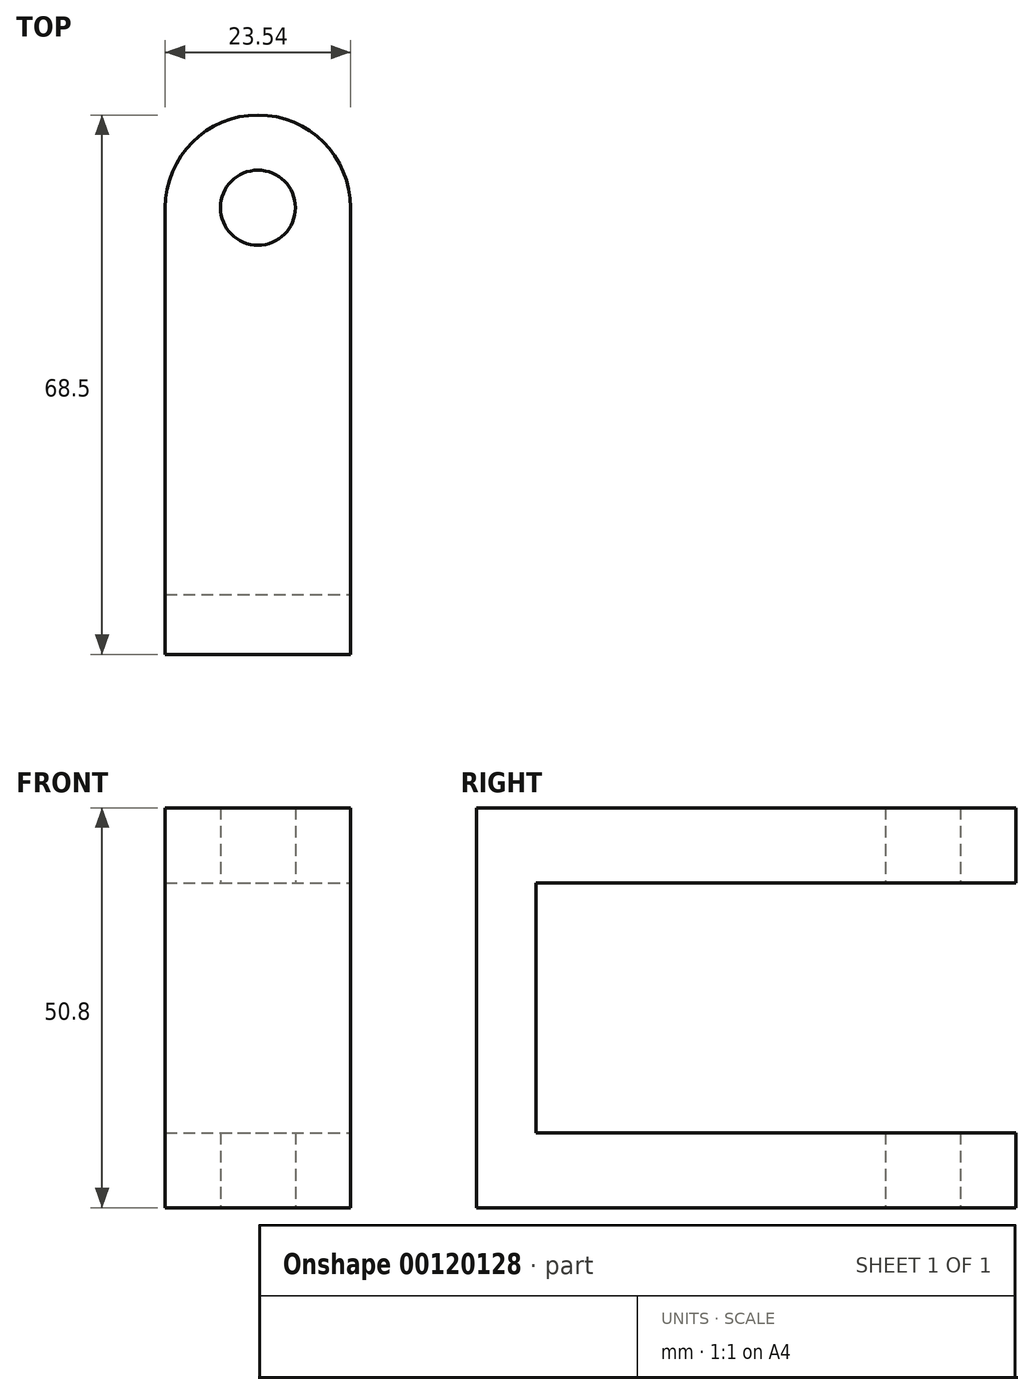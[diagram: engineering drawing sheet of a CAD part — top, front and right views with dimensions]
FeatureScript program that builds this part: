
annotation { "Feature Type Name" : "Feature", "Feature Type Description" : "" }
export const myFeature = defineFeature(function(context is Context, id is Id, definition is map)
    precondition{}
    {
        {
            var Q0;
            Q0=qCreatedBy(makeId("Top.planeOp"),FACE);
            var sketch = newSketch(context, id + "F0", { "sketchPlane" : qUnion([Q0])});
            skLineSegment(sketch, "E0.bottom", {"start": v(-11.77, -56.73) * mm, "end": v(11.77, -56.73) * mm});
            skLineSegment(sketch, "E0.top", {"start": v(-11.77, 0) * mm, "end": v(11.77, 0) * mm, "construction": true});
            skLineSegment(sketch, "E0.left", {"start": v(-11.77, -56.73) * mm, "end": v(-11.77, 0) * mm});
            skLineSegment(sketch, "E0.right", {"start": v(11.77, -56.73) * mm, "end": v(11.77, 0) * mm});
            skArc(sketch, "E1", {"start": v(11.77, 0) * mm, "mid": v(0, 11.77) * mm, "end": v(-11.77, 0) * mm});
            skCircle(sketch, "E2", {"center": v(0, 0) * mm, "radius": 4.76 * mm});
            skSolve(sketch);
        }
        {
            var Q0;
            Q0=makeQuery(id+"F0.imprint","IMPRINT",FACE,{"disambiguationData":[TD([[makeQuery(id+"F0.imprint","IMPRINT",EDGE,{"derivedFrom":sQuery(id+"F0.wireOp",EDGE,"E0.bottom")}),1.0]])]});
            extrude(context, id + "F1", {"entities" : qUnion([Q0]), "depth" : 50.8 * mm});
        }
        {
            var Q0;
            Q0=makeQuery(id+"F1.opExtrude","SWEPT_FACE",FACE,{"disambiguationData":[OSD([sQuery(id+"F0.wireOp",EDGE,"E0.right")])]});
            var sketch = newSketch(context, id + "F2", { "sketchPlane" : qUnion([Q0])});
            skLineSegment(sketch, "E3.bottom", {"start": v(-49.15, 41.28) * mm, "end": v(18.1, 41.28) * mm});
            skLineSegment(sketch, "E3.top", {"start": v(-49.15, 9.52) * mm, "end": v(18.1, 9.52) * mm});
            skLineSegment(sketch, "E3.left", {"start": v(-49.15, 41.28) * mm, "end": v(-49.15, 9.52) * mm});
            skLineSegment(sketch, "E3.right", {"start": v(18.1, 41.28) * mm, "end": v(18.1, 9.52) * mm});
            skLineSegment(sketch, "E4", {"start": v(-35.74, 41.28) * mm, "end": v(-35.74, 50.8) * mm});
            skLineSegment(sketch, "E5", {"start": v(-35.74, 9.52) * mm, "end": v(-35.74, 0) * mm});
            skSolve(sketch);
        }
        {
            var Q0;
            {var subQ4=sQuery(id+"F2.wireOp",EDGE,"E3.left");Q0=makeQuery(id+"F2.imprint","IMPRINT",FACE,{"disambiguationData":[TD([[makeQuery(id+"F2.imprint","IMPRINT",EDGE,{"derivedFrom":subQ4}),1.0]])]});}
            var Q1;
            {var subQ0=sQuery(id+"F2.wireOp",EDGE,"E3.right");Q1=makeQuery(id+"F2.imprint","IMPRINT",FACE,{"disambiguationData":[TD([[makeQuery(id+"F2.imprint","IMPRINT",EDGE,{"derivedFrom":subQ0}),-1.0]])]});}
            extrude(context, id + "F3", {"entities" : qUnion([Q0, Q1]), "operationType" : NewBodyOperationType.REMOVE, "endBound" : BoundingType.THROUGH_ALL, "oppositeDirection" : true, "depth" : 25.4 * mm});
        }
    });
